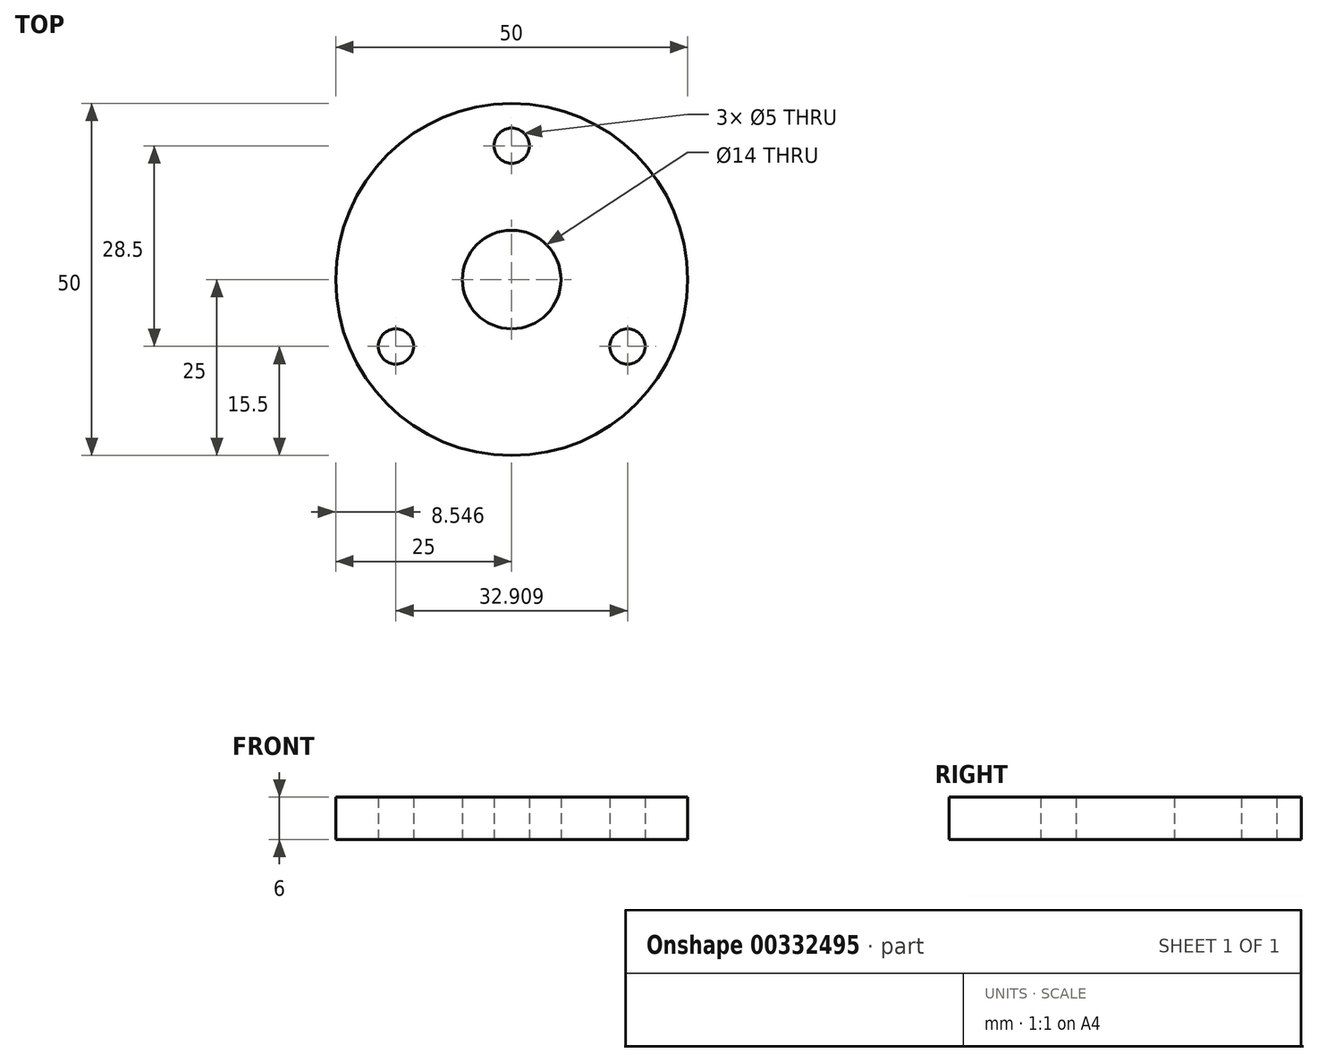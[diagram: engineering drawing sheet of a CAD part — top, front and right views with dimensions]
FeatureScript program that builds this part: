
annotation { "Feature Type Name" : "Feature", "Feature Type Description" : "" }
export const myFeature = defineFeature(function(context is Context, id is Id, definition is map)
    precondition{}
    {
        {
            var Q0;
            Q0=qCreatedBy(makeId("Top.planeOp"),FACE);
            var sketch = newSketch(context, id + "F0", { "sketchPlane" : qUnion([Q0])});
            skCircle(sketch, "E0", {"center": v(0, 0) * mm, "radius": 25 * mm});
            skCircle(sketch, "E1", {"center": v(0, 19) * mm, "radius": 2.5 * mm});
            skCircle(sketch, "E2", {"center": v(-16.45, -9.5) * mm, "radius": 2.5 * mm});
            skCircle(sketch, "E3", {"center": v(16.45, -9.5) * mm, "radius": 2.5 * mm});
            skLineSegment(sketch, "E4", {"start": v(0, 0) * mm, "end": v(-16.45, -9.5) * mm});
            skLineSegment(sketch, "E5", {"start": v(0, 0) * mm, "end": v(16.45, -9.5) * mm});
            skSolve(sketch);
        }
        {
            var Q0;
            Q0 = qSketchRegion(id + "F0", true);
            extrude(context, id + "F1", {"entities" : qUnion([Q0]), "depth" : 6 * mm});
        }
        {
            var Q0;
            Q0=qCreatedBy(makeId("Top.planeOp"),FACE);
            var sketch = newSketch(context, id + "F2", { "sketchPlane" : qUnion([Q0])});
            skCircle(sketch, "E6", {"center": v(0, 0) * mm, "radius": 7 * mm});
            skSolve(sketch);
        }
        {
            var Q0;
            Q0=makeQuery(id+"F2.imprint","IMPRINT",FACE,{"disambiguationData":[TD([[makeQuery(id+"F2.imprint","IMPRINT",EDGE,{"derivedFrom":sQuery(id+"F2.wireOp",EDGE,"E6")}),1.0]])]});
            extrude(context, id + "F3", {"entities" : qUnion([Q0]), "operationType" : NewBodyOperationType.REMOVE, "depth" : 6 * mm});
        }
    });
